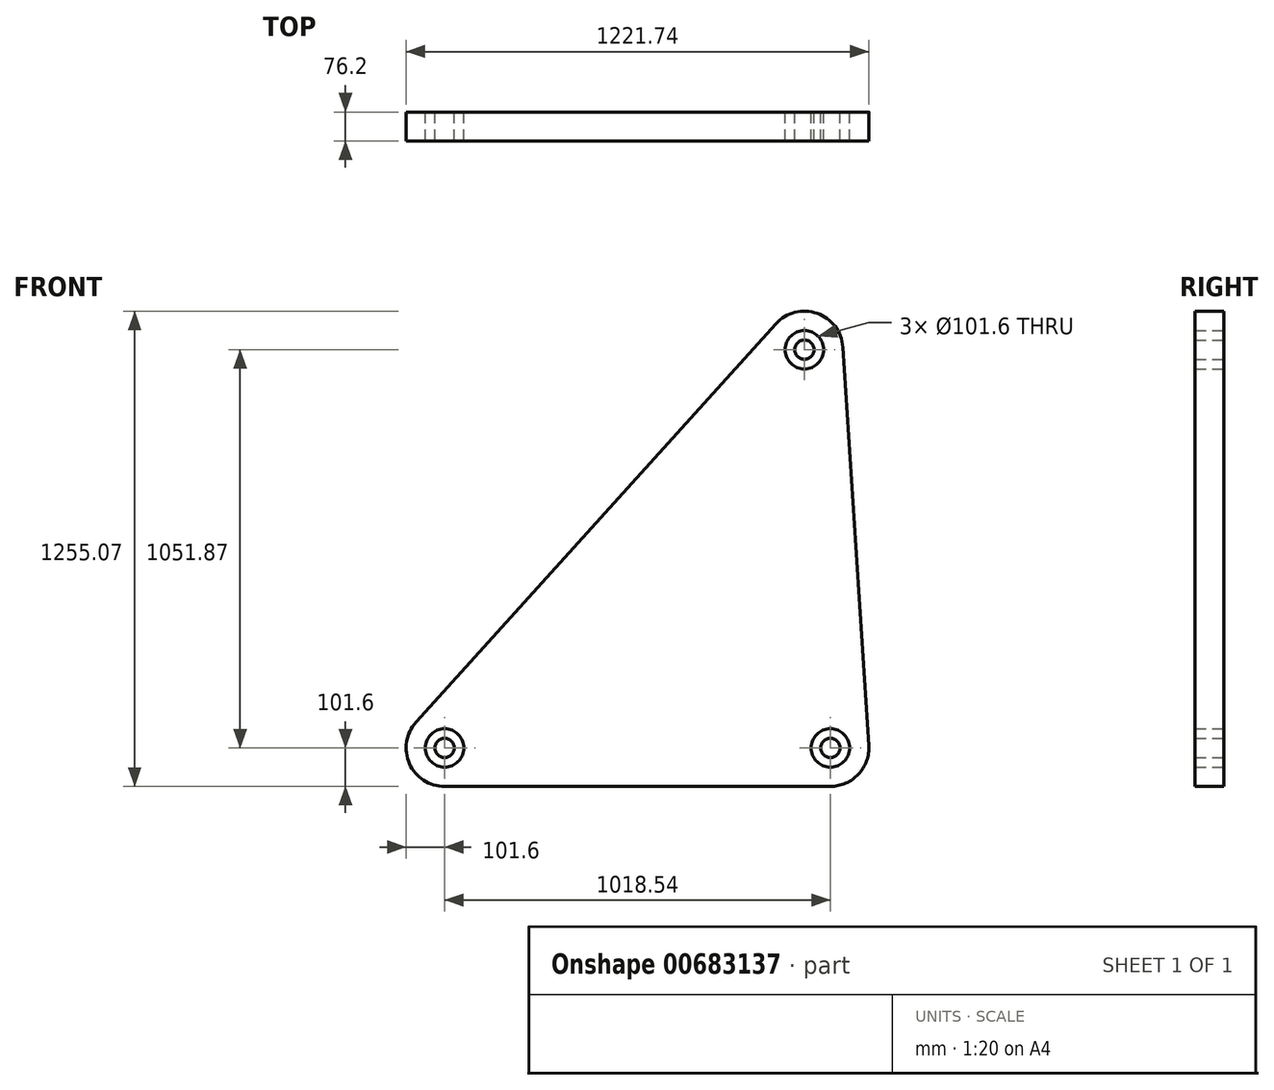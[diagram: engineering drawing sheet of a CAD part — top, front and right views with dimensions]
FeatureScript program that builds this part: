
annotation { "Feature Type Name" : "Feature", "Feature Type Description" : "" }
export const myFeature = defineFeature(function(context is Context, id is Id, definition is map)
    precondition{}
    {
        {
            var Q0;
            Q0=qCreatedBy(makeId("Front.planeOp"),FACE);
            var sketch = newSketch(context, id + "F0", { "sketchPlane" : qUnion([Q0])});
            skLineSegment(sketch, "E0", {"start": v(0, 0) * mm, "end": v(1018.54, 0) * mm});
            skLineSegment(sketch, "E1", {"start": v(1018.54, 0) * mm, "end": v(949.93, 1051.87) * mm});
            skLineSegment(sketch, "E2", {"start": v(949.93, 1051.87) * mm, "end": v(0, 0) * mm});
            skArc(sketch, "E3", {"start": v(-75.4, 68.1) * mm, "mid": v(-92.85, -41.26) * mm, "end": v(0, -101.6) * mm});
            skArc(sketch, "E4", {"start": v(1018.54, -101.6) * mm, "mid": v(1092.68, -69.46) * mm, "end": v(1119.92, 6.61) * mm});
            skArc(sketch, "E5", {"start": v(1051.32, 1058.48) * mm, "mid": v(983.3, 1147.83) * mm, "end": v(874.53, 1119.96) * mm});
            skLineSegment(sketch, "E6.0", {"start": v(1119.92, 6.61) * mm, "end": v(1051.32, 1058.48) * mm});
            skLineSegment(sketch, "E7.0", {"start": v(874.53, 1119.96) * mm, "end": v(-75.4, 68.1) * mm});
            skLineSegment(sketch, "E8.0", {"start": v(0, -101.6) * mm, "end": v(1018.54, -101.6) * mm});
            skCircle(sketch, "E9", {"center": v(949.93, 1051.87) * mm, "radius": 50.8 * mm});
            skCircle(sketch, "E10", {"center": v(1018.54, 0) * mm, "radius": 50.8 * mm});
            skCircle(sketch, "E11", {"center": v(0, 0) * mm, "radius": 50.8 * mm});
            skCircle(sketch, "E12", {"center": v(0, 0) * mm, "radius": 25.4 * mm});
            skCircle(sketch, "E13", {"center": v(1018.54, 0) * mm, "radius": 25.4 * mm});
            skCircle(sketch, "E14", {"center": v(949.93, 1051.87) * mm, "radius": 25.4 * mm});
            skSolve(sketch);
        }
        {
            var Q0;
            Q0 = qSketchRegion(id + "F0", true);
            var Q1;
            {var subQ7=sQuery(id+"F0.wireOp",EDGE,"E11");var subQ9=sQuery(id+"F0.wireOp",EDGE,"E0");var subQ10=makeQuery(id+"F0.imprint","INTERSECT",VERTEX,{"derivedFrom":[subQ9,subQ7]});Q1=makeQuery(id+"F0.imprint","IMPRINT",FACE,{"disambiguationData":[TD([[makeQuery(id+"F0.imprint","IMPRINT",EDGE,{"disambiguationData":[TD([[subQ10,-1.0]])],"derivedFrom":subQ9}),1.0]])]});}
            var Q2;
            {var subQ0=sQuery(id+"F0.wireOp",EDGE,"E2");var subQ1=sQuery(id+"F0.wireOp",EDGE,"E0");var subQ2=makeQuery(id+"F0.imprint","INTERSECT",VERTEX,{"derivedFrom":[subQ1,subQ0]});Q2=makeQuery(id+"F0.imprint","IMPRINT",FACE,{"disambiguationData":[TD([[makeQuery(id+"F0.imprint","IMPRINT",EDGE,{"disambiguationData":[TD([[subQ2,-1.0]])],"derivedFrom":subQ1}),-1.0]])]});}
            var Q3;
            {var subQ0=sQuery(id+"F0.wireOp",EDGE,"E1");var subQ1=sQuery(id+"F0.wireOp",EDGE,"E0");var subQ2=makeQuery(id+"F0.imprint","INTERSECT",VERTEX,{"derivedFrom":[subQ1,subQ0]});Q3=makeQuery(id+"F0.imprint","IMPRINT",FACE,{"disambiguationData":[TD([[makeQuery(id+"F0.imprint","IMPRINT",EDGE,{"disambiguationData":[TD([[subQ2,1.0]])],"derivedFrom":subQ1}),-1.0]])]});}
            var Q4;
            {var subQ0=sQuery(id+"F0.wireOp",EDGE,"E1");var subQ1=sQuery(id+"F0.wireOp",EDGE,"E0");var subQ2=makeQuery(id+"F0.imprint","INTERSECT",VERTEX,{"derivedFrom":[subQ1,subQ0]});Q4=makeQuery(id+"F0.imprint","IMPRINT",FACE,{"disambiguationData":[TD([[makeQuery(id+"F0.imprint","IMPRINT",EDGE,{"disambiguationData":[TD([[subQ2,1.0]])],"derivedFrom":subQ1}),1.0]])]});}
            var Q5;
            {var subQ0=sQuery(id+"F0.wireOp",EDGE,"E2");var subQ1=sQuery(id+"F0.wireOp",EDGE,"E0");var subQ2=makeQuery(id+"F0.imprint","INTERSECT",VERTEX,{"derivedFrom":[subQ1,subQ0]});Q5=makeQuery(id+"F0.imprint","IMPRINT",FACE,{"disambiguationData":[TD([[makeQuery(id+"F0.imprint","IMPRINT",EDGE,{"disambiguationData":[TD([[subQ2,-1.0]])],"derivedFrom":subQ1}),1.0]])]});}
            var Q6;
            {var subQ0=sQuery(id+"F0.wireOp",EDGE,"E2");var subQ1=sQuery(id+"F0.wireOp",EDGE,"E1");var subQ2=makeQuery(id+"F0.imprint","INTERSECT",VERTEX,{"derivedFrom":[subQ1,subQ0]});Q6=makeQuery(id+"F0.imprint","IMPRINT",FACE,{"disambiguationData":[TD([[makeQuery(id+"F0.imprint","IMPRINT",EDGE,{"disambiguationData":[TD([[subQ2,1.0]])],"derivedFrom":subQ1}),1.0]])]});}
            var Q7;
            {var subQ0=sQuery(id+"F0.wireOp",EDGE,"E2");var subQ1=sQuery(id+"F0.wireOp",EDGE,"E1");var subQ2=makeQuery(id+"F0.imprint","INTERSECT",VERTEX,{"derivedFrom":[subQ1,subQ0]});Q7=makeQuery(id+"F0.imprint","IMPRINT",FACE,{"disambiguationData":[TD([[makeQuery(id+"F0.imprint","IMPRINT",EDGE,{"disambiguationData":[TD([[subQ2,1.0]])],"derivedFrom":subQ1}),-1.0]])]});}
            extrude(context, id + "F1", {"entities" : qUnion([Q0, Q1, Q2, Q3, Q4, Q5, Q6, Q7]), "depth" : 76.2 * mm, "offsetDistance" : 25.4 * mm});
        }
    });
